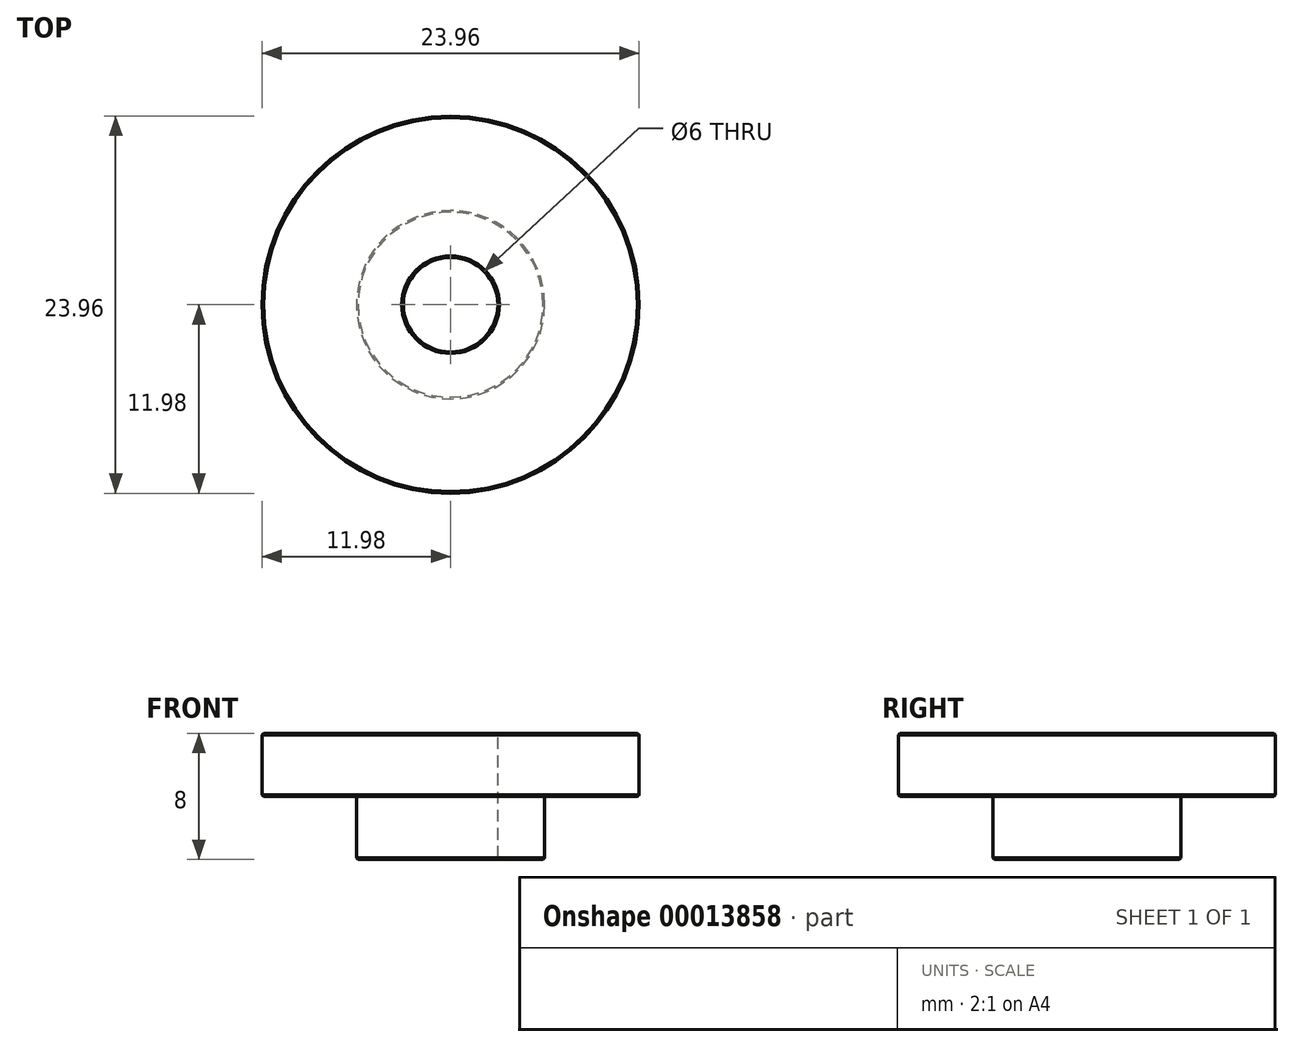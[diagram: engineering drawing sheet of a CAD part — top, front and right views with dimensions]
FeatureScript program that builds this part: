
annotation { "Feature Type Name" : "Feature", "Feature Type Description" : "" }
export const myFeature = defineFeature(function(context is Context, id is Id, definition is map)
    precondition{}
    {
        {
            var Q0;
            Q0=qCreatedBy(makeId("Top.planeOp"),FACE);
            var sketch = newSketch(context, id + "F0", { "sketchPlane" : qUnion([Q0])});
            skCircle(sketch, "E0", {"center": v(0, 0) * mm, "radius": 11.97 * mm});
            skCircle(sketch, "E1", {"center": v(0, 0) * mm, "radius": 5.97 * mm});
            skCircle(sketch, "E2", {"center": v(0, 0) * mm, "radius": 3 * mm});
            skSolve(sketch);
        }
        {
            var Q0;
            Q0=makeQuery(id+"F0.imprint","IMPRINT",FACE,{"disambiguationData":[TD([[makeQuery(id+"F0.imprint","IMPRINT",EDGE,{"derivedFrom":sQuery(id+"F0.wireOp",EDGE,"E0")}),1.0]])]});
            var Q1;
            Q1=makeQuery(id+"F0.imprint","IMPRINT",FACE,{"disambiguationData":[TD([[makeQuery(id+"F0.imprint","IMPRINT",EDGE,{"derivedFrom":sQuery(id+"F0.wireOp",EDGE,"E1")}),1.0]])]});
            extrude(context, id + "F1", {"entities" : qUnion([Q0, Q1]), "oppositeDirection" : true, "depth" : 4 * mm});
        }
        {
            var Q0;
            Q0=makeQuery(id+"F0.imprint","IMPRINT",FACE,{"disambiguationData":[TD([[makeQuery(id+"F0.imprint","IMPRINT",EDGE,{"derivedFrom":sQuery(id+"F0.wireOp",EDGE,"E1")}),1.0]])]});
            extrude(context, id + "F2", {"entities" : qUnion([Q0]), "operationType" : NewBodyOperationType.ADD, "oppositeDirection" : true, "depth" : 8 * mm});
        }
        {
            var Q0;
            Q0=makeQuery(id+"F1.opExtrude","CAP_FACE",FACE,{"disambiguationData":[OSD([sQuery(id+"F0.wireOp",EDGE,"E0"),sQuery(id+"F0.wireOp",EDGE,"E2")])],"isStart":true});
            var Q1;
            Q1=makeQuery(id+"F1.opExtrude","SWEPT_FACE",FACE,{"disambiguationData":[OSD([sQuery(id+"F0.wireOp",EDGE,"E0")])]});
            var Q2;
            {var subQ0=sQuery(id+"F0.wireOp",EDGE,"E2");Q2=makeQuery(id+"F2.boolean.opBoolean","MERGE",FACE,{"derivedFrom":[makeQuery(id+"F1.opExtrude","SWEPT_FACE",FACE,{"disambiguationData":[OSD([subQ0])]}),makeQuery(id+"F2.opExtrude","SWEPT_FACE",FACE,{"disambiguationData":[OSD([subQ0])]})]});}
            var Q3;
            Q3=makeQuery(id+"F2.opExtrude","CAP_FACE",FACE,{"disambiguationData":[OSD([sQuery(id+"F0.wireOp",EDGE,"E1"),sQuery(id+"F0.wireOp",EDGE,"E2")])],"isStart":false});
            chamfer(context, id + "F3", {"entities" : qUnion([Q0, Q1, Q2, Q3]), "width" : .1 * mm, "tangentPropagation" : true});
        }
    });
